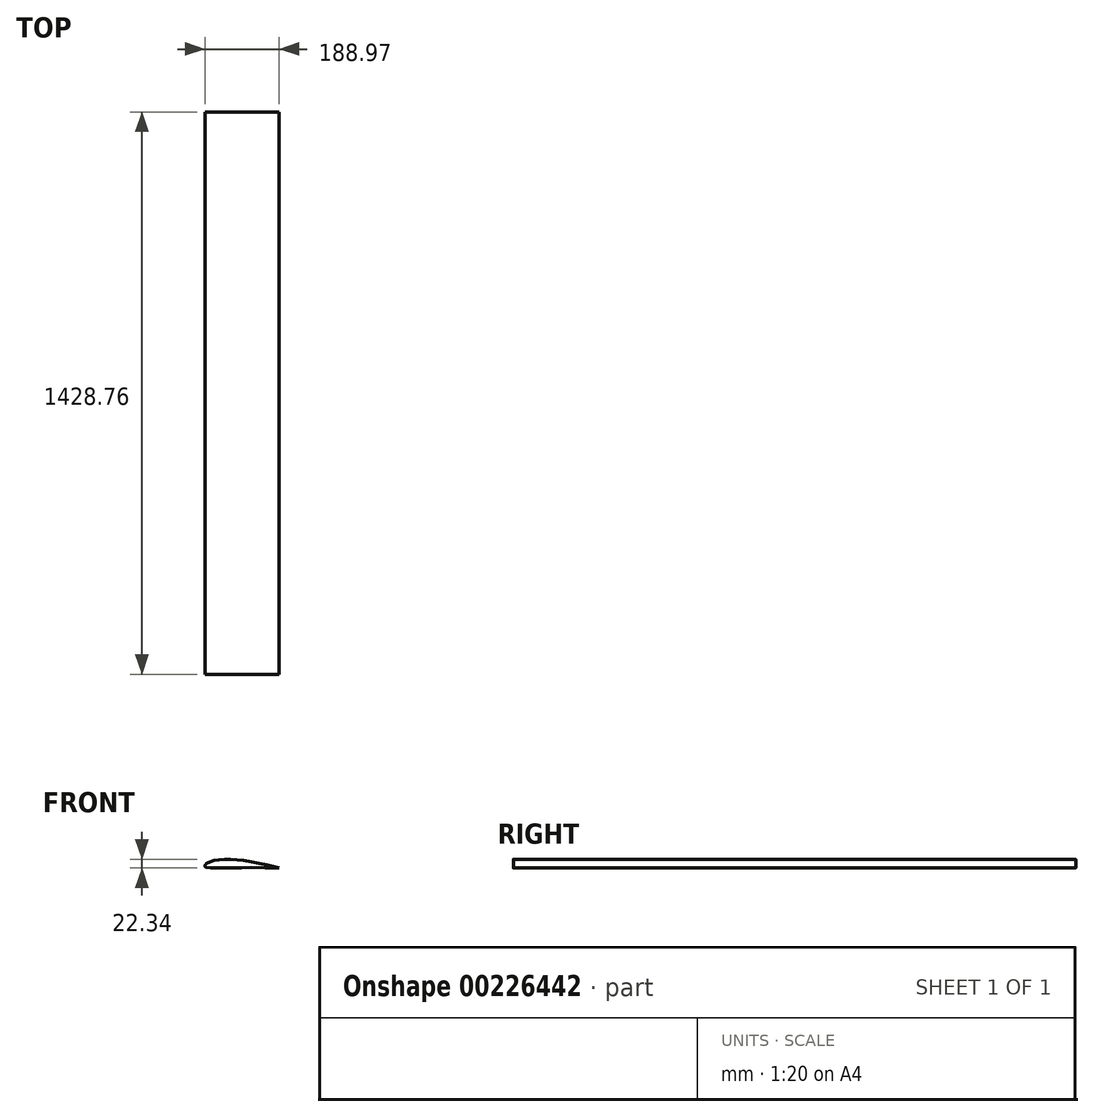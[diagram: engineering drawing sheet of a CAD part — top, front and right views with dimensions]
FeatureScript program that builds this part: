
annotation { "Feature Type Name" : "Feature", "Feature Type Description" : "" }
export const myFeature = defineFeature(function(context is Context, id is Id, definition is map)
    precondition{}
    {
        {
            var Q0;
            Q0=qCreatedBy(makeId("Front.planeOp"),FACE);
            var sketch = newSketch(context, id + "F0", { "sketchPlane" : qUnion([Q0])});
            skFitSpline(sketch, "E0.0", {"points": [v(330.51, -26.8) * mm, v(330.41, -27.02) * mm, v(320.9, -26.65) * mm, v(282.9, -25.74) * mm, v(133.46, -23.45) * mm, v(-1.4, -24.3) * mm, v(-5.52, -24.35) * mm, v(-223.27, -27.63) * mm, v(-263.84, -26.15) * mm, v(-289.63, -25.37) * mm, v(-306.1, -22.64) * mm, v(-310.34, -21.37) * mm, v(-312.97, -20.17) * mm, v(-315.36, -18.5) * mm, v(-317.44, -16.46) * mm, v(-318.92, -14.43) * mm, v(-319.94, -12.57) * mm, v(-320.57, -10.76) * mm, v(-320.82, -9.61) * mm, v(-320.99, -7.97) * mm, v(-320.86, -6.28) * mm, v(-320.4, -4.3) * mm, v(-319.53, -2.04) * mm, v(-317.5, 1.34) * mm, v(-314.64, 4.78) * mm, v(-309.38, 9.62) * mm, v(-300.92, 15.27) * mm, v(-284.86, 23.88) * mm, v(-268.85, 30.71) * mm, v(-251.3, 35.74) * mm, v(-225.1, 41.46) * mm, v(-196.52, 45.77) * mm, v(-164.68, 48.46) * mm, v(-128.36, 49.34) * mm, v(-84.95, 48.6) * mm, v(-42.8, 45.45) * mm, v(0.59, 40.3) * mm, v(69.38, 29.76) * mm, v(139.47, 17.63) * mm, v(201.78, 4.38) * mm, v(277.63, -13.26) * mm, v(320.71, -24.55) * mm, v(330.61, -26.58) * mm, v(330.51, -26.8) * mm]});
            skPoint(sketch, "E1", {"position": v(330.51, -26.8) * mm});
            skPoint(sketch, "E2", {"position": v(-320.85, -9.19) * mm});
            skSolve(sketch);
        }
        {
            var Q0;
            Q0=makeQuery(id+"F0.imprint","IMPRINT",FACE,{"disambiguationData":[TD([[makeQuery(id+"F0.imprint","IMPRINT",EDGE,{"derivedFrom":sQuery(id+"F0.wireOp",EDGE,"E0.0")}),-1.0]])]});
            extrude(context, id + "F1", {"entities" : qUnion([Q0]), "depth" : 635 * mm, "offsetDistance" : 25.4 * mm, "symmetric" : true});
        }
        {
            var Q0;
            Q0=makeQuery(id+"F1.opExtrude","SWEPT_BODY",BODY,{"disambiguationData":[OSD([sQuery(id+"F0.wireOp",EDGE,"E0.0")])]});
            var Q1;
            Q1=qCreatedBy(makeId("Origin.pointOp"),VERTEX);
            transform(context, id + "F2", {"entities" : qUnion([Q0]), "transformType" : TransformType.SCALE_UNIFORMLY, "scale" : .29, "scalePoint" : qUnion([Q1]), "makeCopy" : false});
        }
        {
            var Q0;
            Q0=makeQuery(id+"F1.opExtrude","CAP_FACE",FACE,{"disambiguationData":[OSD([sQuery(id+"F0.wireOp",EDGE,"E0.0")])],"isStart":true});
            extrude(context, id + "F3", {"entities" : qUnion([Q0]), "operationType" : NewBodyOperationType.ADD, "depth" : 1244.6 * mm, "offsetDistance" : 25.4 * mm});
        }
    });
